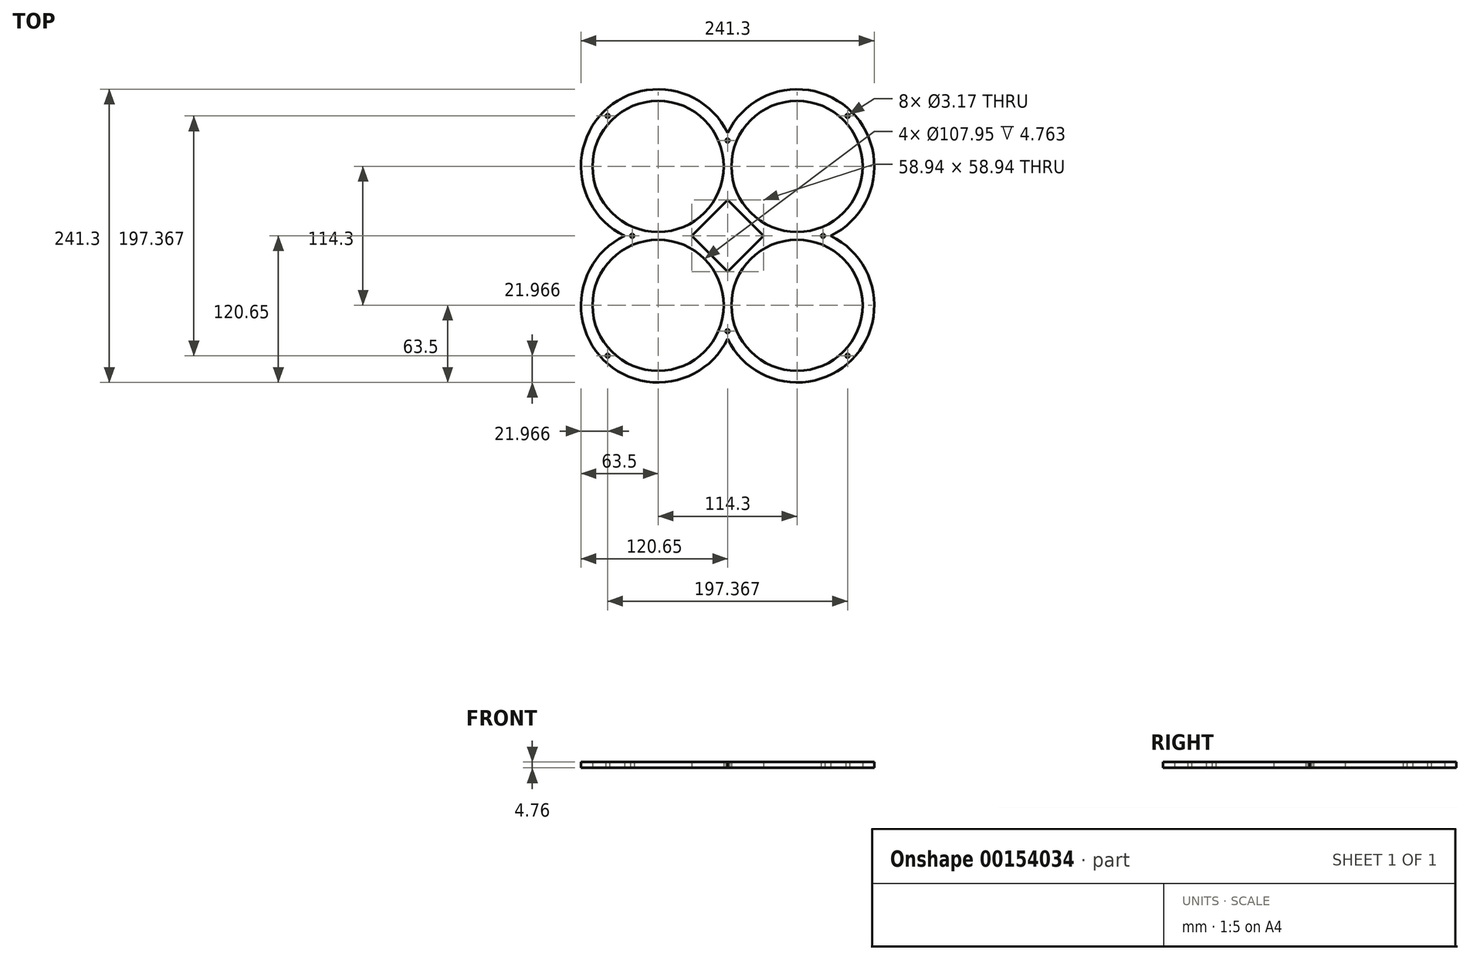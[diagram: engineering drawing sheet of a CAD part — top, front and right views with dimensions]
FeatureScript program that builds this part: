
annotation { "Feature Type Name" : "Feature", "Feature Type Description" : "" }
export const myFeature = defineFeature(function(context is Context, id is Id, definition is map)
    precondition{}
    {
        {
            var Q0;
            Q0=qCreatedBy(makeId("Top.planeOp"),FACE);
            var sketch = newSketch(context, id + "F0", { "sketchPlane" : qUnion([Q0])});
            skPoint(sketch, "E0.middle", {"position": v(0, 0) * mm});
            skCircle(sketch, "E1", {"center": v(-57.15, 57.15) * mm, "radius": 53.98 * mm});
            skCircle(sketch, "E2", {"center": v(57.15, 57.15) * mm, "radius": 53.98 * mm});
            skCircle(sketch, "E3", {"center": v(57.15, -57.15) * mm, "radius": 53.98 * mm});
            skCircle(sketch, "E4", {"center": v(-57.15, -57.15) * mm, "radius": 53.98 * mm});
            skArc(sketch, "E5", {"start": v(0, 84.83) * mm, "mid": v(-102.05, 102.05) * mm, "end": v(-84.83, 0) * mm});
            skLineSegment(sketch, "E6", {"start": v(0, 0) * mm, "end": v(0, 29.47) * mm});
            skLineSegment(sketch, "E7", {"start": v(0, 29.47) * mm, "end": v(-29.47, 0) * mm});
            skLineSegment(sketch, "E8", {"start": v(-29.47, 0) * mm, "end": v(0, -29.47) * mm});
            skLineSegment(sketch, "E9", {"start": v(0, -29.47) * mm, "end": v(29.47, 0) * mm});
            skLineSegment(sketch, "E10", {"start": v(29.47, 0) * mm, "end": v(0, 29.47) * mm});
            skArc(sketch, "E11.trimOffspring", {"start": v(-84.83, 0) * mm, "mid": v(-102.05, -102.05) * mm, "end": v(0, -84.83) * mm});
            skArc(sketch, "E12.trimOffspring", {"start": v(84.83, 0) * mm, "mid": v(102.05, 102.05) * mm, "end": v(0, 84.83) * mm});
            skArc(sketch, "E13.trimOffspring", {"start": v(0, -84.83) * mm, "mid": v(102.05, -102.05) * mm, "end": v(84.83, 0) * mm});
            skLineSegment(sketch, "E14", {"start": v(98.68, 98.68) * mm, "end": v(102.05, 102.05) * mm});
            skLineSegment(sketch, "E15", {"start": v(102.05, 102.05) * mm, "end": v(98.68, 98.68) * mm});
            skLineSegment(sketch, "E16", {"start": v(-102.05, -102.05) * mm, "end": v(-95.32, -95.32) * mm});
            skLineSegment(sketch, "E17", {"start": v(102.05, -102.05) * mm, "end": v(95.32, -95.32) * mm});
            skLineSegment(sketch, "E18", {"start": v(-102.05, 102.05) * mm, "end": v(-98.68, 98.68) * mm});
            skLineSegment(sketch, "E19.trimOffspring", {"start": v(-98.68, 98.68) * mm, "end": v(-102.05, 102.05) * mm});
            skLineSegment(sketch, "E20.trimOffspring", {"start": v(-95.32, -95.32) * mm, "end": v(-102.05, -102.05) * mm});
            skLineSegment(sketch, "E21.trimOffspring", {"start": v(95.32, -95.32) * mm, "end": v(102.05, -102.05) * mm});
            skPoint(sketch, "E22.orphan", {"position": v(95.32, 95.32) * mm});
            skLineSegment(sketch, "E23", {"start": v(102.05, -102.05) * mm, "end": v(98.68, -98.68) * mm});
            skLineSegment(sketch, "E24", {"start": v(-102.05, -102.05) * mm, "end": v(-98.68, -98.68) * mm});
            skLineSegment(sketch, "E25", {"start": v(-84.83, 0) * mm, "end": v(-78.48, 0) * mm});
            skLineSegment(sketch, "E26", {"start": v(0, -84.83) * mm, "end": v(0, -78.48) * mm});
            skLineSegment(sketch, "E27", {"start": v(84.83, 0) * mm, "end": v(78.48, 0) * mm});
            skLineSegment(sketch, "E28", {"start": v(0, 84.83) * mm, "end": v(0, 78.48) * mm});
            skSolve(sketch);
        }
        {
            var Q0;
            Q0=makeQuery(id+"F0.imprint","IMPRINT",FACE,{"disambiguationData":[TD([[makeQuery(id+"F0.imprint","IMPRINT",EDGE,{"derivedFrom":sQuery(id+"F0.wireOp",EDGE,"E1")}),-1.0]])]});
            extrude(context, id + "F1", {"entities" : qUnion([Q0]), "depth" : 4.76 * mm});
        }
        {
            var Q0;
            Q0=sQuery(id+"F0.wireOp",VERTEX,"E24.end");
            var Q1;
            Q1=sQuery(id+"F0.wireOp",VERTEX,"E25.end");
            var Q2;
            Q2=sQuery(id+"F0.wireOp",VERTEX,"E18.end");
            var Q3;
            Q3=sQuery(id+"F0.wireOp",VERTEX,"E28.end");
            var Q4;
            Q4=sQuery(id+"F0.wireOp",VERTEX,"E14.start");
            var Q5;
            Q5=sQuery(id+"F0.wireOp",VERTEX,"E27.end");
            var Q6;
            Q6=sQuery(id+"F0.wireOp",VERTEX,"E23.end");
            var Q7;
            Q7=sQuery(id+"F0.wireOp",VERTEX,"E26.end");
            var Q8;
            Q8=makeQuery(id+"F1.opExtrude","SWEPT_BODY",BODY,{"disambiguationData":[OSD([sQuery(id+"F0.wireOp",EDGE,"E1"),sQuery(id+"F0.wireOp",EDGE,"E2"),sQuery(id+"F0.wireOp",EDGE,"E3"),sQuery(id+"F0.wireOp",EDGE,"E4"),sQuery(id+"F0.wireOp",EDGE,"E5"),sQuery(id+"F0.wireOp",EDGE,"E7"),sQuery(id+"F0.wireOp",EDGE,"E8"),sQuery(id+"F0.wireOp",EDGE,"E9"),sQuery(id+"F0.wireOp",EDGE,"E10"),sQuery(id+"F0.wireOp",EDGE,"E11.trimOffspring"),sQuery(id+"F0.wireOp",EDGE,"E12.trimOffspring"),sQuery(id+"F0.wireOp",EDGE,"E13.trimOffspring")])]});
            hole(context, id + "F2", {"style" : HoleStyle.SIMPLE, "endStyle" : HoleEndStyle.BLIND, "oppositeDirection" : true, "holeDiameter" : 3.17 * mm, "holeDepth" : 9.52 * mm, "locations" : qUnion([Q0, Q1, Q2, Q3, Q4, Q5, Q6, Q7]), "scope" : qUnion([Q8])});
        }
    });
